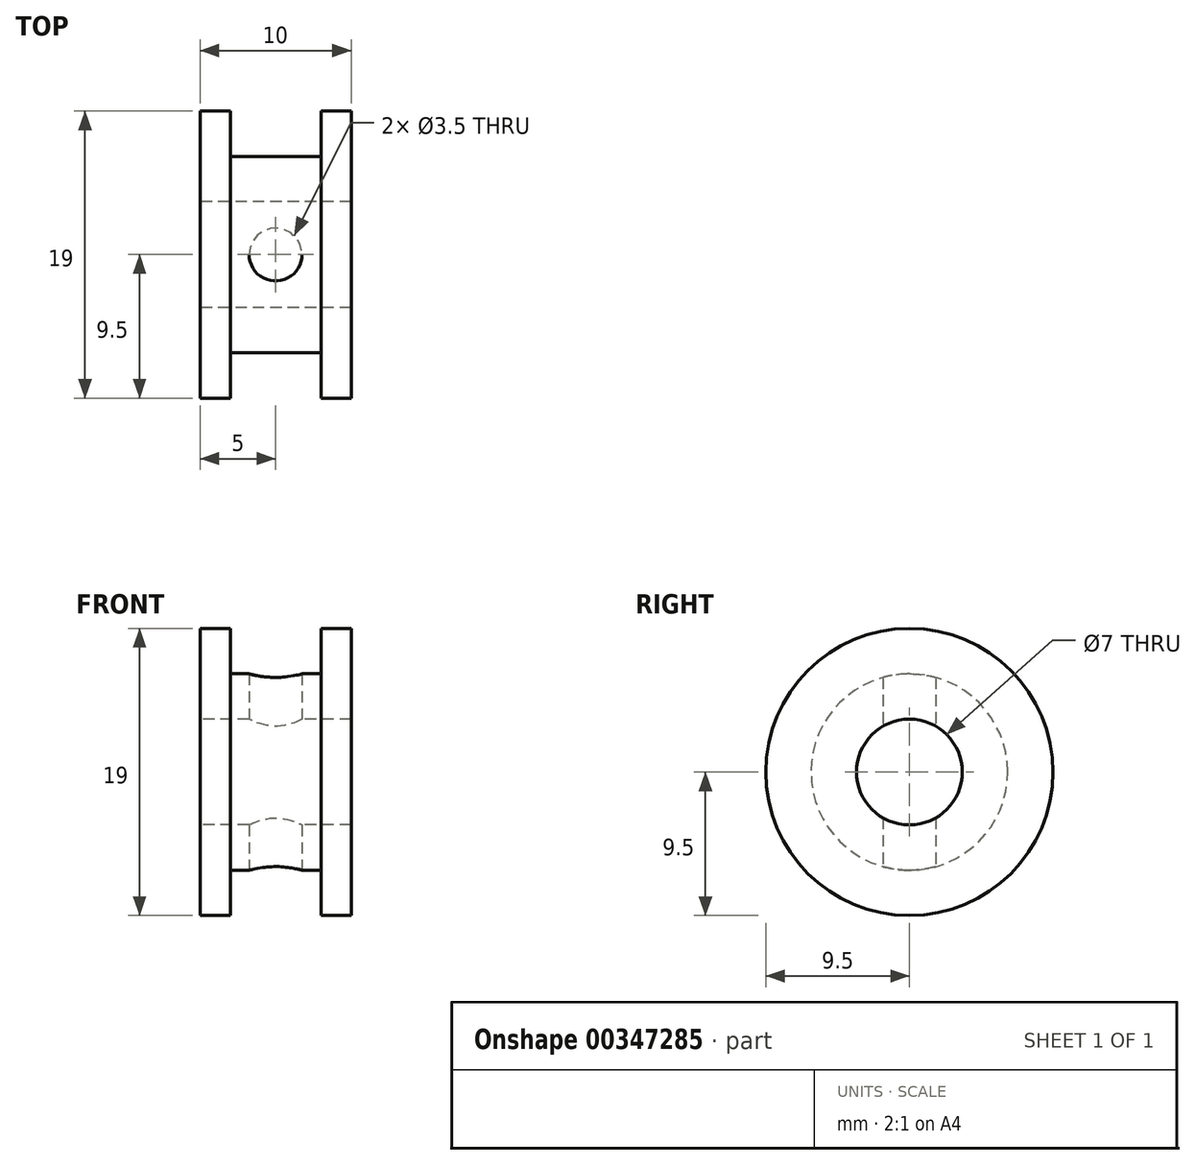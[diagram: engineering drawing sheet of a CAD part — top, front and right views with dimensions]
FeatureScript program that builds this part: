
annotation { "Feature Type Name" : "Feature", "Feature Type Description" : "" }
export const myFeature = defineFeature(function(context is Context, id is Id, definition is map)
    precondition{}
    {
        {
            var Q0;
            Q0=qCreatedBy(makeId("Top.planeOp"),FACE);
            var sketch = newSketch(context, id + "F0", { "sketchPlane" : qUnion([Q0])});
            skLineSegment(sketch, "E0.bottom", {"start": v(-5, 0) * mm, "end": v(5, 0) * mm, "construction": true});
            skLineSegment(sketch, "E0.left", {"start": v(-5, 0) * mm, "end": v(-5, 3.5) * mm, "construction": true});
            skLineSegment(sketch, "E0.right", {"start": v(5, 0) * mm, "end": v(5, 3.5) * mm, "construction": true});
            skLineSegment(sketch, "E1", {"start": v(-5, 3.5) * mm, "end": v(-5, 9.5) * mm});
            skLineSegment(sketch, "E2", {"start": v(-5, 9.5) * mm, "end": v(-3, 9.5) * mm});
            skLineSegment(sketch, "E3", {"start": v(-3, 9.5) * mm, "end": v(-3, 6.5) * mm});
            skLineSegment(sketch, "E4", {"start": v(-3, 6.5) * mm, "end": v(3, 6.5) * mm});
            skLineSegment(sketch, "E5", {"start": v(3, 6.5) * mm, "end": v(3, 9.5) * mm});
            skLineSegment(sketch, "E6", {"start": v(3, 9.5) * mm, "end": v(5, 9.5) * mm});
            skLineSegment(sketch, "E7", {"start": v(5, 9.5) * mm, "end": v(5, 3.5) * mm});
            skLineSegment(sketch, "E8", {"start": v(-5, 3.5) * mm, "end": v(5, 3.5) * mm});
            skPoint(sketch, "E9", {"position": v(0, 0) * mm});
            skSolve(sketch);
        }
        {
            var Q0;
            Q0=makeQuery(id+"F0.imprint","IMPRINT",FACE,{"disambiguationData":[TD([[makeQuery(id+"F0.imprint","IMPRINT",EDGE,{"derivedFrom":sQuery(id+"F0.wireOp",EDGE,"E1")}),-1.0]])]});
            var Q1;
            Q1=sQuery(id+"F0.wireOp",EDGE,"E0.bottom");
            revolve(context, id + "F1", {"entities" : qUnion([Q0]), "axis" : qUnion([Q1]), "revolveType" : RevolveType.FULL});
        }
        {
            var Q0;
            Q0=qCreatedBy(makeId("Top.planeOp"),FACE);
            var sketch = newSketch(context, id + "F2", { "sketchPlane" : qUnion([Q0])});
            skCircle(sketch, "E10", {"center": v(0, 0) * mm, "radius": 1.75 * mm});
            skSolve(sketch);
        }
        {
            var Q0;
            Q0 = qSketchRegion(id + "F2", true);
            extrude(context, id + "F3", {"entities" : qUnion([Q0]), "operationType" : NewBodyOperationType.REMOVE, "endBound" : BoundingType.THROUGH_ALL, "depth" : 25 * mm, "hasSecondDirection" : true, "secondDirectionBound" : SecondDirectionBoundingType.THROUGH_ALL, "secondDirectionOppositeDirection" : true, "secondDirectionDepth" : 25 * mm});
        }
    });
